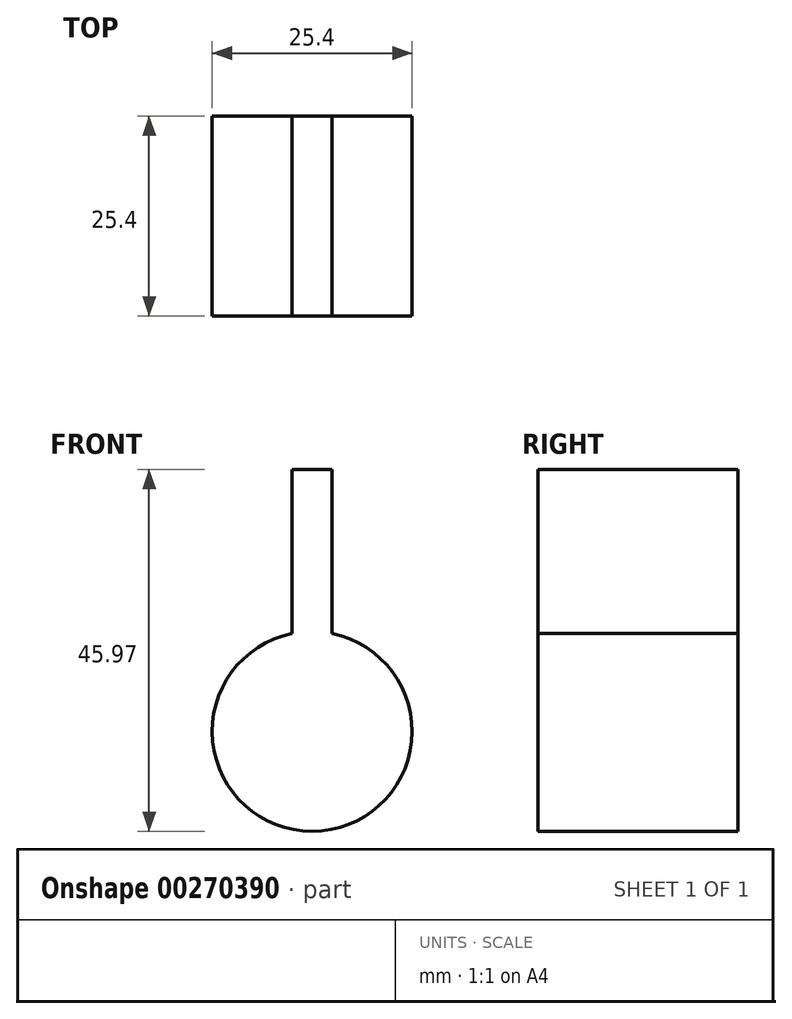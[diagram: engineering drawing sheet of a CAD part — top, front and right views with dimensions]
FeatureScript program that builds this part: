
annotation { "Feature Type Name" : "Feature", "Feature Type Description" : "" }
export const myFeature = defineFeature(function(context is Context, id is Id, definition is map)
    precondition{}
    {
        {
            var Q0;
            Q0=qCreatedBy(makeId("Front.planeOp"),FACE);
            var sketch = newSketch(context, id + "F0", { "sketchPlane" : qUnion([Q0])});
            skCircle(sketch, "E0", {"center": v(0, 0) * mm, "radius": 12.7 * mm});
            skLineSegment(sketch, "E1.bottom", {"start": v(-2.54, 0) * mm, "end": v(2.54, 0) * mm});
            skLineSegment(sketch, "E1.top", {"start": v(-2.54, 33.27) * mm, "end": v(2.54, 33.27) * mm});
            skLineSegment(sketch, "E1.left", {"start": v(-2.54, 0) * mm, "end": v(-2.54, 33.27) * mm});
            skLineSegment(sketch, "E1.right", {"start": v(2.54, 0) * mm, "end": v(2.54, 33.27) * mm});
            skSolve(sketch);
        }
        {
            var Q0;
            Q0=makeQuery(id+"F0.imprint","IMPRINT",FACE,{"disambiguationData":[TD([[makeQuery(id+"F0.imprint","IMPRINT",EDGE,{"derivedFrom":sQuery(id+"F0.wireOp",EDGE,"E0")}),1.0]])]});
            extrude(context, id + "F1", {"entities" : qUnion([Q0]), "depth" : 25.4 * mm});
        }
        {
            var Q0;
            {var subQ5=sQuery(id+"F0.wireOp",EDGE,"E1.top");Q0=makeQuery(id+"F0.imprint","IMPRINT",FACE,{"disambiguationData":[TD([[makeQuery(id+"F0.imprint","IMPRINT",EDGE,{"derivedFrom":subQ5}),-1.0]])]});}
            var Q1;
            {var subQ5=sQuery(id+"F0.wireOp",EDGE,"E1.bottom");Q1=makeQuery(id+"F0.imprint","IMPRINT",FACE,{"disambiguationData":[TD([[makeQuery(id+"F0.imprint","IMPRINT",EDGE,{"derivedFrom":subQ5}),1.0]])]});}
            var Q2;
            Q2=makeQuery(id+"F1.opExtrude","CAP_FACE",FACE,{"disambiguationData":[OSD([sQuery(id+"F0.wireOp",EDGE,"E0")])],"isStart":false});
            extrude(context, id + "F2", {"entities" : qUnion([Q0, Q1]), "operationType" : NewBodyOperationType.ADD, "endBound" : BoundingType.UP_TO_SURFACE, "endBoundEntityFace" : qUnion([Q2]), "depth" : 5.08 * mm});
        }
    });
